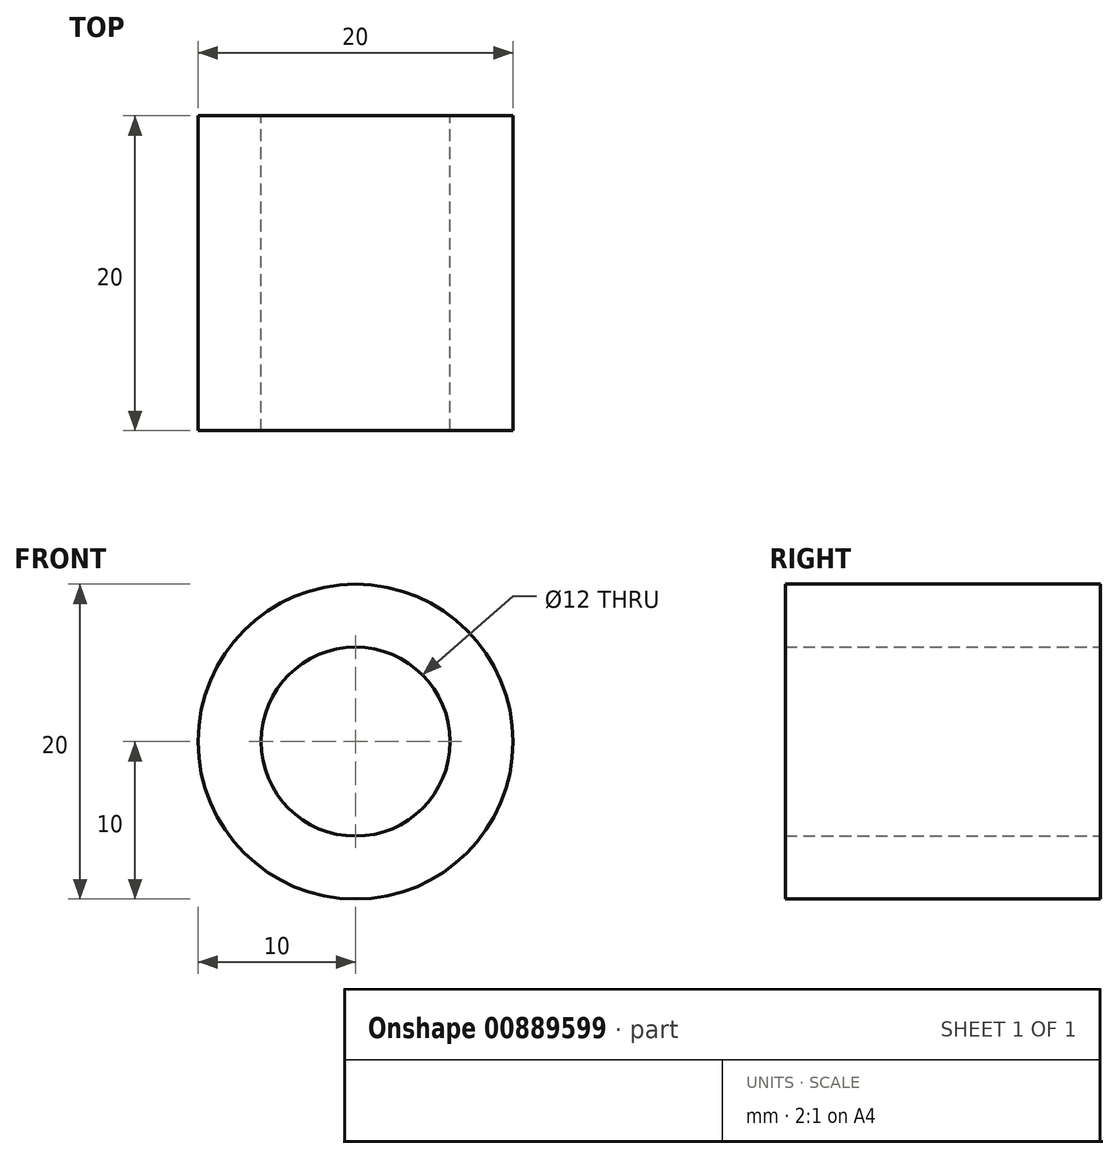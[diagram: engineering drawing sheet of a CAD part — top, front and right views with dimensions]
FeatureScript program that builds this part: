
annotation { "Feature Type Name" : "Feature", "Feature Type Description" : "" }
export const myFeature = defineFeature(function(context is Context, id is Id, definition is map)
    precondition{}
    {
        {
            var Q0;
            Q0=qCreatedBy(makeId("Front.planeOp"),FACE);
            var sketch = newSketch(context, id + "F0", { "sketchPlane" : qUnion([Q0])});
            skCircle(sketch, "E0", {"center": v(0, 0) * mm, "radius": 6 * mm});
            skCircle(sketch, "E1", {"center": v(0, 0) * mm, "radius": 10 * mm});
            skSolve(sketch);
        }
        {
            var Q0;
            Q0=makeQuery(id+"F0.imprint","IMPRINT",FACE,{"disambiguationData":[TD([[makeQuery(id+"F0.imprint","IMPRINT",EDGE,{"derivedFrom":sQuery(id+"F0.wireOp",EDGE,"E0")}),-1.0]])]});
            extrude(context, id + "F1", {"entities" : qUnion([Q0]), "depth" : 20 * mm, "offsetDistance" : 25 * mm});
        }
    });
